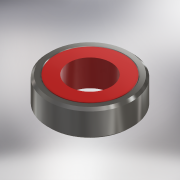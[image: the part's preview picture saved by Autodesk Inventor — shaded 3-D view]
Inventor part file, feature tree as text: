
AUTODESK INVENTOR PART (.ipt)
format: ipt  version: 2017 (Build 210142000, 142)  size: 149,504 bytes
history: native  units: mm
features: extrude x2, chamfer x2, sketch x2
ambient origin geometry x8: Origin, YZ Plane, XZ Plane, XY Plane, X Axis, Y Axis, Z Axis, Center Point
bodies: Solid1 (feature_tree), Solid2 (feature_tree)
feature tree (6):
  extrude  "Extrusion1"  Depth=7.0mm
  chamfer  "Chamfer1"  Distance=7.0mm
  extrude  "Extrusion2"  Depth=11.0mm
  chamfer  "Chamfer2"  Distance=7.0mm
  sketch  "Sketch1"  dims[d0=22.0mm d1=18.0mm d2=7.0mm d3=0.0mm]
  sketch  "Sketch2"  dims[d4=0.6mm d5=2.0mm d6=45.0deg d7=11.0mm d8=7.0mm d9=0.0mm d10=0.2mm d11=2.0mm d12=45.0deg]
